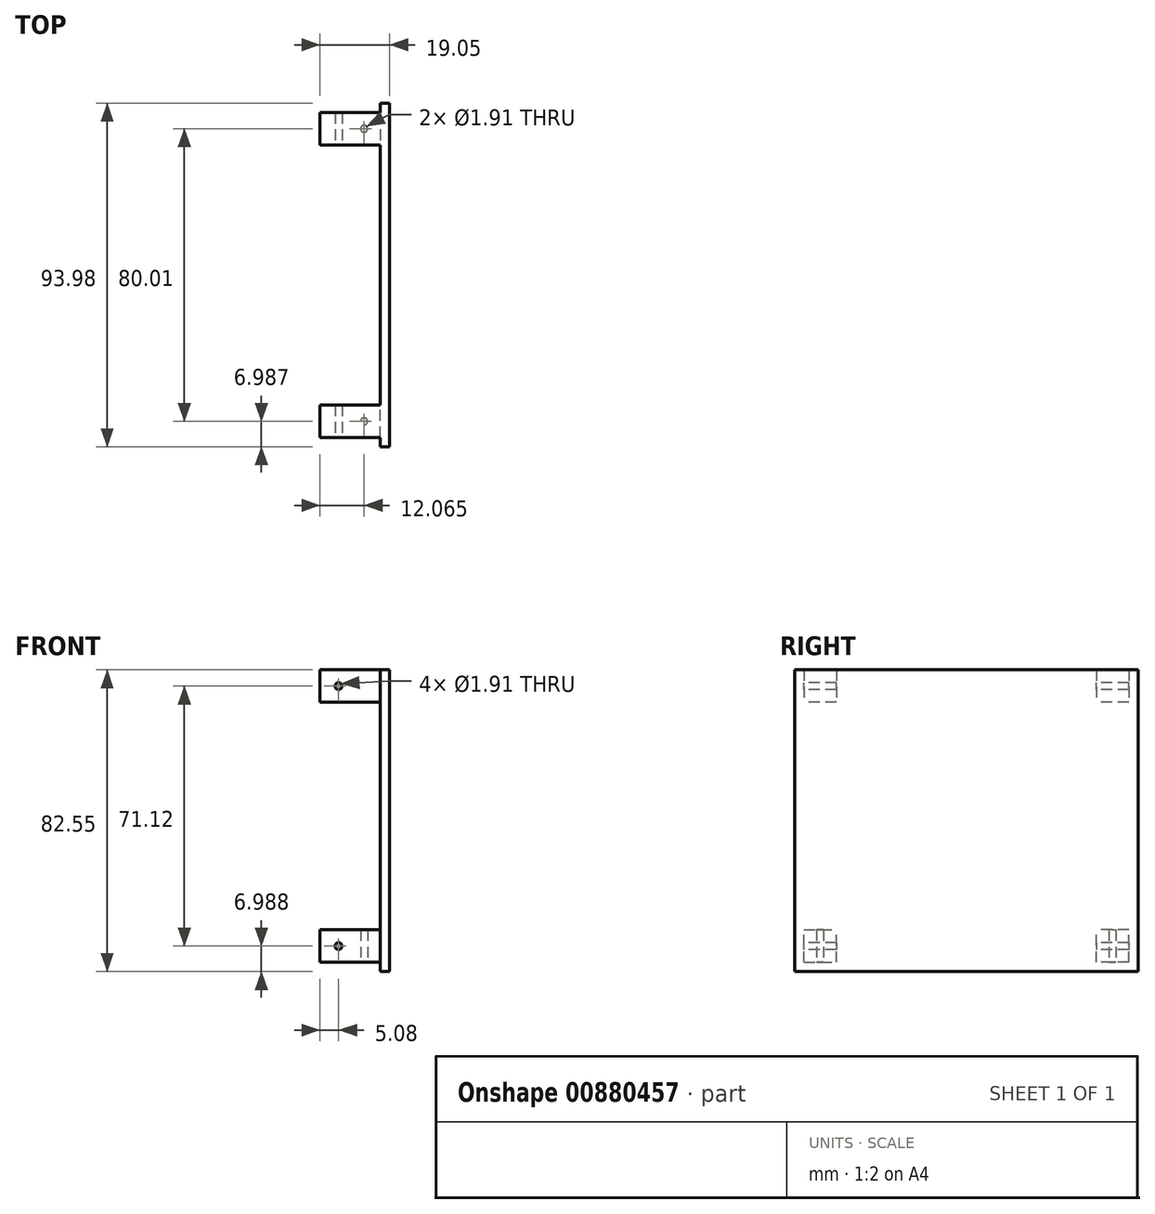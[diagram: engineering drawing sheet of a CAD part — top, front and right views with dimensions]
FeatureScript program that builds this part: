
annotation { "Feature Type Name" : "Feature", "Feature Type Description" : "" }
export const myFeature = defineFeature(function(context is Context, id is Id, definition is map)
    precondition{}
    {
        {
            var Q0;
            Q0=qCreatedBy(makeId("Right.planeOp"),FACE);
            var sketch = newSketch(context, id + "F0", { "sketchPlane" : qUnion([Q0])});
            skLineSegment(sketch, "E0.bottom", {"start": v(-39.88, 39.35) * mm, "end": v(54.1, 39.35) * mm});
            skLineSegment(sketch, "E0.top", {"start": v(-39.88, -43.2) * mm, "end": v(54.1, -43.2) * mm});
            skLineSegment(sketch, "E0.left", {"start": v(-39.88, 39.35) * mm, "end": v(-39.88, -43.2) * mm});
            skLineSegment(sketch, "E0.right", {"start": v(54.1, 39.35) * mm, "end": v(54.1, -43.2) * mm});
            skSolve(sketch);
        }
        {
            var Q0;
            Q0 = qSketchRegion(id + "F0", true);
            extrude(context, id + "F1", {"entities" : qUnion([Q0]), "depth" : 2.54 * mm, "offsetDistance" : 25.4 * mm});
        }
        {
            var Q0;
            Q0=makeQuery(id+"F1.opExtrude","CAP_FACE",FACE,{"disambiguationData":[OSD([sQuery(id+"F0.wireOp",EDGE,"E0.bottom"),sQuery(id+"F0.wireOp",EDGE,"E0.top"),sQuery(id+"F0.wireOp",EDGE,"E0.left"),sQuery(id+"F0.wireOp",EDGE,"E0.right")])],"isStart":true});
            var sketch = newSketch(context, id + "F2", { "sketchPlane" : qUnion([Q0])});
            skLineSegment(sketch, "E1.bottom", {"start": v(-51.56, 39.35) * mm, "end": v(-42.67, 39.35) * mm});
            skLineSegment(sketch, "E1.top", {"start": v(-51.56, 30.46) * mm, "end": v(-42.67, 30.46) * mm});
            skLineSegment(sketch, "E1.left", {"start": v(-51.56, 39.35) * mm, "end": v(-51.56, 30.46) * mm});
            skLineSegment(sketch, "E1.right", {"start": v(-42.67, 39.35) * mm, "end": v(-42.67, 30.46) * mm});
            skLineSegment(sketch, "E2.bottom", {"start": v(28.45, 39.35) * mm, "end": v(37.34, 39.35) * mm});
            skLineSegment(sketch, "E2.top", {"start": v(28.45, 30.46) * mm, "end": v(37.34, 30.46) * mm});
            skLineSegment(sketch, "E2.left", {"start": v(28.45, 39.35) * mm, "end": v(28.45, 30.46) * mm});
            skLineSegment(sketch, "E2.right", {"start": v(37.34, 39.35) * mm, "end": v(37.34, 30.46) * mm});
            skLineSegment(sketch, "E3.bottom", {"start": v(37.34, -40.66) * mm, "end": v(28.45, -40.66) * mm});
            skLineSegment(sketch, "E3.top", {"start": v(37.34, -31.77) * mm, "end": v(28.45, -31.77) * mm});
            skLineSegment(sketch, "E3.left", {"start": v(37.34, -40.66) * mm, "end": v(37.34, -31.77) * mm});
            skLineSegment(sketch, "E3.right", {"start": v(28.45, -40.66) * mm, "end": v(28.45, -31.77) * mm});
            skLineSegment(sketch, "E4.bottom", {"start": v(-51.56, -40.66) * mm, "end": v(-42.67, -40.66) * mm});
            skLineSegment(sketch, "E4.top", {"start": v(-51.56, -31.77) * mm, "end": v(-42.67, -31.77) * mm});
            skLineSegment(sketch, "E4.left", {"start": v(-51.56, -40.66) * mm, "end": v(-51.56, -31.77) * mm});
            skLineSegment(sketch, "E4.right", {"start": v(-42.67, -40.66) * mm, "end": v(-42.67, -31.77) * mm});
            skSolve(sketch);
        }
        {
            var Q0;
            Q0 = qSketchRegion(id + "F2", true);
            extrude(context, id + "F3", {"entities" : qUnion([Q0]), "operationType" : NewBodyOperationType.ADD, "depth" : 16.5 * mm, "offsetDistance" : 25.4 * mm});
        }
        {
            var Q0;
            Q0=makeQuery(id+"F3.opExtrude","SWEPT_FACE",FACE,{"disambiguationData":[OSD([sQuery(id+"F2.wireOp",EDGE,"E2.right")])]});
            var sketch = newSketch(context, id + "F4", { "sketchPlane" : qUnion([Q0])});
            skPoint(sketch, "E5", {"position": v(-11.43, 34.9) * mm});
            skPoint(sketch, "E5.positionSnap0", {"position": v(-16.51, 34.9) * mm});
            skSolve(sketch);
        }
        {
            var Q0;
            Q0=makeQuery(id+"F3.opExtrude","SWEPT_FACE",FACE,{"disambiguationData":[OSD([sQuery(id+"F2.wireOp",EDGE,"E3.left")])]});
            var sketch = newSketch(context, id + "F5", { "sketchPlane" : qUnion([Q0])});
            skPoint(sketch, "E6", {"position": v(-16.51, -36.21) * mm});
            skPoint(sketch, "E7", {"position": v(-11.43, -36.21) * mm});
            skSolve(sketch);
        }
        {
            var Q0;
            Q0=sQuery(id+"F5.wireOp",VERTEX,"E7");
            var Q1;
            Q1=sQuery(id+"F4.wireOp",VERTEX,"E5");
            var Q2;
            Q2=makeQuery(id+"F1.opExtrude","SWEPT_BODY",BODY,{"disambiguationData":[OSD([sQuery(id+"F0.wireOp",EDGE,"E0.bottom"),sQuery(id+"F0.wireOp",EDGE,"E0.top"),sQuery(id+"F0.wireOp",EDGE,"E0.left"),sQuery(id+"F0.wireOp",EDGE,"E0.right")])]});
            hole(context, id + "F6", {"style" : HoleStyle.SIMPLE, "endStyle" : HoleEndStyle.THROUGH, "holeDiameter" : 1.9 * mm, "majorDiameter" : 6.35 * mm, "isTappedThrough" : true, "tappedDepth" : 12.7 * mm, "tapClearance" : 3, "locations" : qUnion([Q0, Q1]), "scope" : qUnion([Q2])});
        }
        {
            var Q0;
            Q0=makeQuery(id+"F3.opExtrude","SWEPT_FACE",FACE,{"disambiguationData":[OSD([sQuery(id+"F2.wireOp",EDGE,"E4.bottom")])]});
            var sketch = newSketch(context, id + "F7", { "sketchPlane" : qUnion([Q0])});
            skPoint(sketch, "E8", {"position": v(-4.45, -47.12) * mm});
            skPoint(sketch, "E8.positionSnap0", {"position": v(0, -47.12) * mm});
            skSolve(sketch);
        }
        {
            var Q0;
            Q0=makeQuery(id+"F3.opExtrude","SWEPT_FACE",FACE,{"disambiguationData":[OSD([sQuery(id+"F2.wireOp",EDGE,"E3.bottom")])]});
            var sketch = newSketch(context, id + "F8", { "sketchPlane" : qUnion([Q0])});
            skPoint(sketch, "E9", {"position": v(-4.45, 32.9) * mm});
            skPoint(sketch, "E9.positionSnap0", {"position": v(0, 32.9) * mm});
            skSolve(sketch);
        }
        {
            var Q0;
            Q0=sQuery(id+"F7.wireOp",VERTEX,"E8");
            var Q1;
            Q1=sQuery(id+"F8.wireOp",VERTEX,"E9");
            var Q2;
            Q2=makeQuery(id+"F1.opExtrude","SWEPT_BODY",BODY,{"disambiguationData":[OSD([sQuery(id+"F0.wireOp",EDGE,"E0.bottom"),sQuery(id+"F0.wireOp",EDGE,"E0.top"),sQuery(id+"F0.wireOp",EDGE,"E0.left"),sQuery(id+"F0.wireOp",EDGE,"E0.right")])]});
            hole(context, id + "F9", {"style" : HoleStyle.SIMPLE, "endStyle" : HoleEndStyle.BLIND, "holeDiameter" : 1.9 * mm, "majorDiameter" : 6.35 * mm, "holeDepth" : 12.7 * mm, "isTappedThrough" : true, "tappedDepth" : 12.7 * mm, "tapClearance" : 3, "locations" : qUnion([Q0, Q1]), "scope" : qUnion([Q2])});
        }
    });
